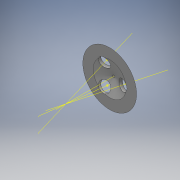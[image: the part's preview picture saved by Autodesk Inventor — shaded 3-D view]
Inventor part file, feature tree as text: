
AUTODESK INVENTOR PART (.ipt)
format: ipt  version: 2016 (Build 200138000, 138)  size: 145,408 bytes
history: native  units: mm
features: other x9, sketch x2, revolve x1, plane x1, extrude x1, pattern_circular x1
ambient origin geometry x8: Origin, YZ Plane, XZ Plane, XY Plane, X Axis, Y Axis, Z Axis, Center Point
bodies: Body1 (feature_tree)
feature tree (15):
  revolve  "Revolution1"  Angle=15.0deg
  plane  "Work Plane2"
  extrude  "Extrusion2"  Depth=0.5mm
  pattern_circular  "Circular Pattern3"  Angle=90.0deg  [1 undecoded]
  other  "Work Axis1"
  other  "Work Point1"
  other  "Work Axis2"
  other  "Work Point2"
  other  "Work Point3"
  other  "Work Axis3"
  other  "Work Axis4"
  other  "Work Axis5"
  other  "Work Axis6"
  sketch  "Sketch1"  dims[d2=5.0mm d3=15.0deg]
  sketch  "Sketch5"  dims[d4=75.0deg d16=0.5mm d17=90.0deg d18=2.0mm d19=0.0mm d20=0.0mm d21=30.0mm d22=360.0deg]
note: 1 required parameter value undecoded (feature->parameter linkage not recoverable at this tier; creation-order binding heuristic only, values carry confidence <= 0.55)
